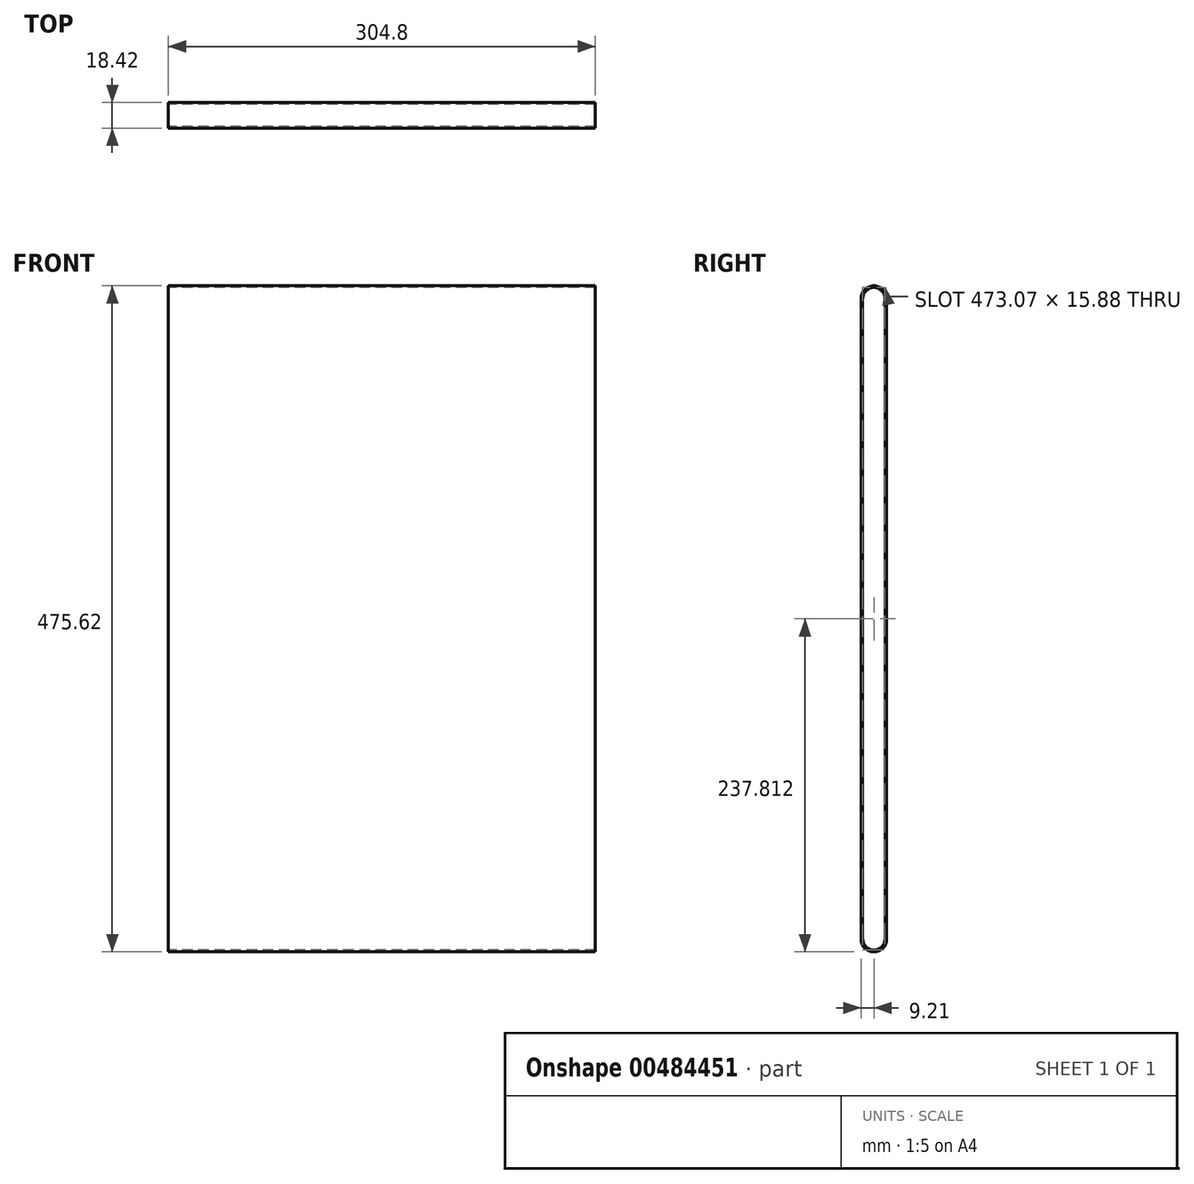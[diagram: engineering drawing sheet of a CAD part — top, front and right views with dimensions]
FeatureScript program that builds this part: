
annotation { "Feature Type Name" : "Feature", "Feature Type Description" : "" }
export const myFeature = defineFeature(function(context is Context, id is Id, definition is map)
    precondition{}
    {
        {
            var Q0;
            Q0=qCreatedBy(makeId("Right.planeOp"),FACE);
            var sketch = newSketch(context, id + "F0", { "sketchPlane" : qUnion([Q0])});
            skArc(sketch, "E0", {"start": v(7.94, 253.88) * mm, "mid": v(0, 261.82) * mm, "end": v(-7.94, 253.88) * mm});
            skArc(sketch, "E1", {"start": v(-7.94, -203.32) * mm, "mid": v(0, -211.26) * mm, "end": v(7.94, -203.32) * mm});
            skLineSegment(sketch, "E2", {"start": v(-7.94, 253.88) * mm, "end": v(-7.94, -203.32) * mm});
            skLineSegment(sketch, "E3", {"start": v(7.94, 253.88) * mm, "end": v(7.94, -203.32) * mm});
            skLineSegment(sketch, "E4.0", {"start": v(-9.2, 253.88) * mm, "end": v(-9.2, -203.32) * mm});
            skLineSegment(sketch, "E5.0", {"start": v(9.2, 253.88) * mm, "end": v(9.2, -203.32) * mm});
            skArc(sketch, "E6.0", {"start": v(-9.2, -203.32) * mm, "mid": v(0, -212.53) * mm, "end": v(9.2, -203.32) * mm});
            skArc(sketch, "E7.0", {"start": v(9.2, 253.88) * mm, "mid": v(0, 263.09) * mm, "end": v(-9.2, 253.88) * mm});
            skSolve(sketch);
        }
        {
            var Q0;
            Q0=makeQuery(id+"F0.imprint","IMPRINT",FACE,{"disambiguationData":[TD([[makeQuery(id+"F0.imprint","IMPRINT",EDGE,{"derivedFrom":sQuery(id+"F0.wireOp",EDGE,"E0")}),-1.0]])]});
            extrude(context, id + "F1", {"entities" : qUnion([Q0]), "depth" : 304.8 * mm});
        }
    });
